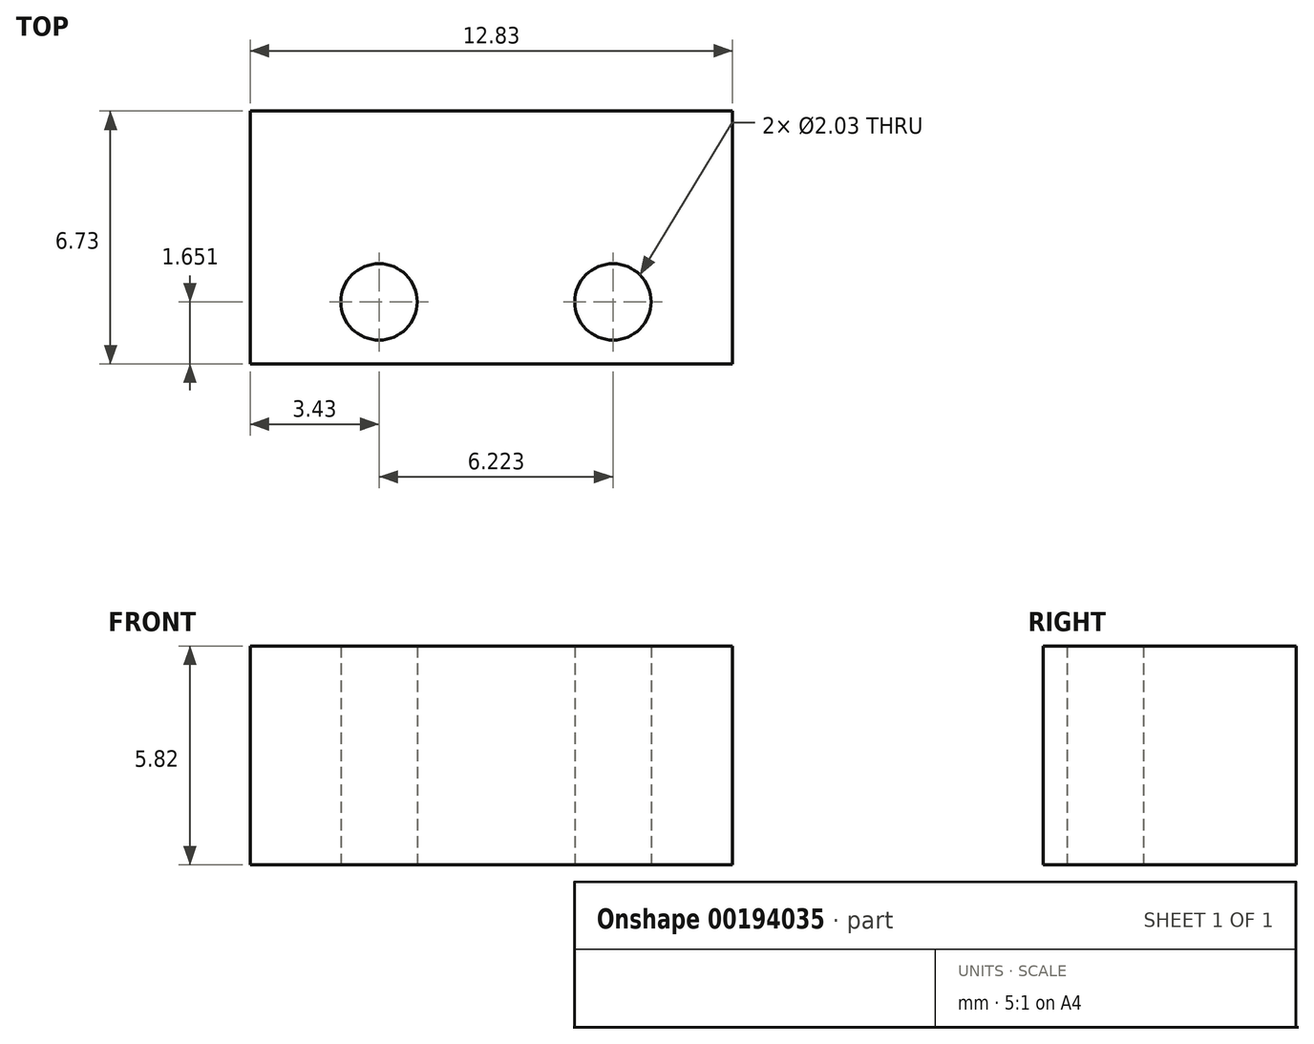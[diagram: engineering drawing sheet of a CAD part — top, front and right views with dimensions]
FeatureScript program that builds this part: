
annotation { "Feature Type Name" : "Feature", "Feature Type Description" : "" }
export const myFeature = defineFeature(function(context is Context, id is Id, definition is map)
    precondition{}
    {
        {
            var Q0;
            Q0=qCreatedBy(makeId("Top.planeOp"),FACE);
            var sketch = newSketch(context, id + "F0", { "sketchPlane" : qUnion([Q0])});
            skLineSegment(sketch, "E0.bottom", {"start": v(-5.5, 2.15) * mm, "end": v(7.33, 2.15) * mm});
            skLineSegment(sketch, "E0.top", {"start": v(-5.5, -4.58) * mm, "end": v(7.33, -4.58) * mm});
            skLineSegment(sketch, "E0.left", {"start": v(-5.5, 2.15) * mm, "end": v(-5.5, -4.58) * mm});
            skLineSegment(sketch, "E0.right", {"start": v(7.33, 2.15) * mm, "end": v(7.33, -4.58) * mm});
            skCircle(sketch, "E1", {"center": v(-2.07, -2.93) * mm, "radius": 1.02 * mm});
            skCircle(sketch, "E2", {"center": v(4.15, -2.93) * mm, "radius": 1.02 * mm});
            skSolve(sketch);
        }
        {
            var Q0;
            Q0 = qSketchRegion(id + "F0", true);
            extrude(context, id + "F1", {"entities" : qUnion([Q0]), "depth" : 5.82 * mm});
        }
    });
